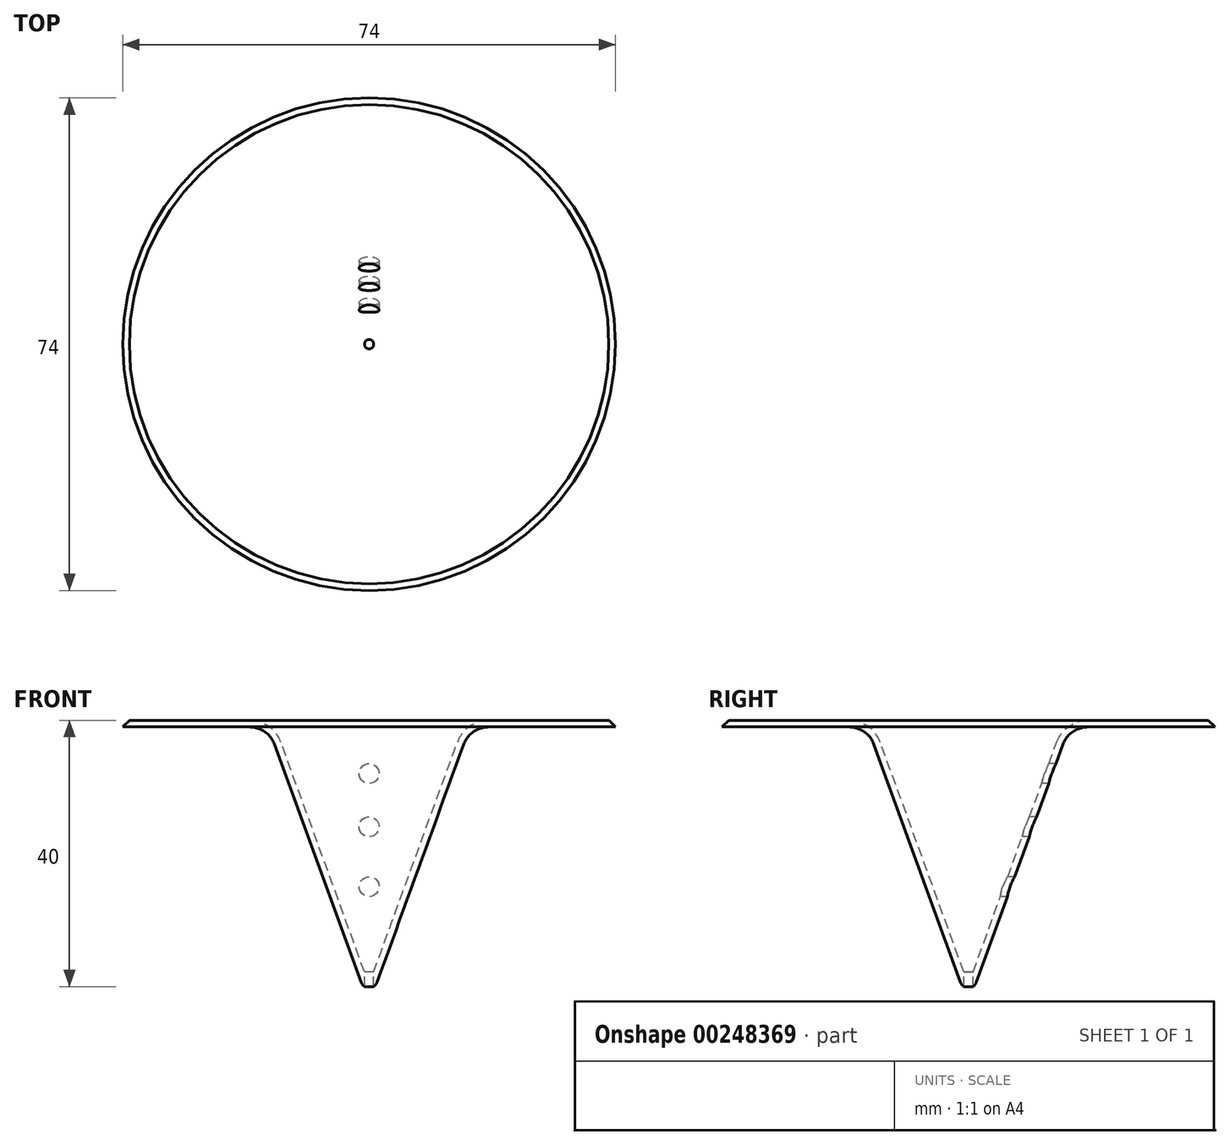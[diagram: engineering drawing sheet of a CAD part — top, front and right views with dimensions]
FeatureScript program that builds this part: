
annotation { "Feature Type Name" : "Feature", "Feature Type Description" : "" }
export const myFeature = defineFeature(function(context is Context, id is Id, definition is map)
    precondition{}
    {
        {
            var Q0;
            Q0=qCreatedBy(makeId("Front.planeOp"),FACE);
            var sketch = newSketch(context, id + "F0", { "sketchPlane" : qUnion([Q0])});
            skLineSegment(sketch, "E0", {"start": v(-36, 1) * mm, "end": v(-37, 0) * mm});
            skLineSegment(sketch, "E1", {"start": v(-37, 0) * mm, "end": v(-17.95, 0) * mm});
            skLineSegment(sketch, "E2", {"start": v(-36, 1) * mm, "end": v(-37, 1) * mm, "construction": true});
            skLineSegment(sketch, "E3", {"start": v(-37, 1) * mm, "end": v(-37, 0) * mm, "construction": true});
            skLineSegment(sketch, "E4.trimOffspring", {"start": v(-17.95, 1) * mm, "end": v(-36, 1) * mm});
            skArc(sketch, "E5", {"start": v(-1.17, -38.39) * mm, "mid": v(-0.98, -38.73) * mm, "end": v(-0.7, -39) * mm});
            skLineSegment(sketch, "E6", {"start": v(0, -34.13) * mm, "end": v(0, -39.21) * mm});
            skLineSegment(sketch, "E7", {"start": v(-0.7, -36.78) * mm, "end": v(-13.25, -2.29) * mm});
            skLineSegment(sketch, "E8", {"start": v(-1.17, -38.39) * mm, "end": v(-14.19, -2.63) * mm});
            skPoint(sketch, "E9.visualSharp", {"position": v(-15.15, 0) * mm});
            skArc(sketch, "E9.filletArc", {"start": v(-14.19, -2.63) * mm, "mid": v(-15.65, -0.72) * mm, "end": v(-17.95, 0) * mm});
            skPoint(sketch, "E10.visualSharp", {"position": v(-14.45, 1) * mm});
            skArc(sketch, "E10.filletArc", {"start": v(-13.25, -2.29) * mm, "mid": v(-15.08, 0.1) * mm, "end": v(-17.95, 1) * mm});
            skLineSegment(sketch, "E11", {"start": v(-0.7, -36.78) * mm, "end": v(-0.7, -39) * mm});
            skSolve(sketch);
        }
        {
            var Q0;
            Q0 = qSketchRegion(id + "F0", true);
            var Q1;
            Q1=sQuery(id+"F0.wireOp",EDGE,"E6");
            revolve(context, id + "F1", {"entities" : qUnion([Q0]), "axis" : qUnion([Q1]), "revolveType" : RevolveType.FULL});
        }
        {
            var Q0;
            Q0=qCreatedBy(makeId("Front.planeOp"),FACE);
            var sketch = newSketch(context, id + "F2", { "sketchPlane" : qUnion([Q0])});
            skPoint(sketch, "E12", {"position": v(0, -7) * mm});
            skPoint(sketch, "E13", {"position": v(0, -15) * mm});
            skPoint(sketch, "E14", {"position": v(0, -23) * mm});
            skSolve(sketch);
        }
        {
            var Q0;
            Q0=sQuery(id+"F2.wireOp",VERTEX,"E12");
            var Q1;
            Q1=makeQuery(id+"F1.opRevolve","SWEPT_BODY",BODY,{"disambiguationData":[OSD([sQuery(id+"F0.wireOp",EDGE,"E0"),sQuery(id+"F0.wireOp",EDGE,"E1"),sQuery(id+"F0.wireOp",EDGE,"yChOrPg3-cPpm-Jh2U-GKyL-P4V1HaA0gBOr"),sQuery(id+"F0.wireOp",EDGE,"y4288l65-jYWD-z8UQ-ppUS-tLJqPGtI5XHZ"),sQuery(id+"F0.wireOp",EDGE,"JWE7uGzO-epyR-hSJP-RyyS-bABGlfE59ylt"),sQuery(id+"F0.wireOp",EDGE,"iOWQaLnk-FQV4-ur3H-6gPm-ICKGlc5A2Xpd"),sQuery(id+"F0.wireOp",EDGE,"KzDe4Qk1-xao2-viCX-nbg6-8rSiEGRuAt0v"),sQuery(id+"F0.wireOp",EDGE,"b27d7dc2-f4b6-4ca7-adcb-c142e029c6df.trimOffspring"),sQuery(id+"F0.wireOp",EDGE,"ad9f041a-46d9-4f32-ac37-72ff34ba22ea.filletArc"),sQuery(id+"F0.wireOp",EDGE,"1201348b-4cfc-4bf2-a3ae-67f3a93fcbf4.filletArc"),sQuery(id+"F0.wireOp",EDGE,"f59c0a59-bad8-41fa-9d51-29288c238455.filletArc"),sQuery(id+"F0.wireOp",EDGE,"5a073df5-ce1a-4d9e-9ccd-e940f481835a.filletArc"),sQuery(id+"F0.wireOp",EDGE,"0fd173fc-3cb6-4043-b6d9-18548de36d7c.0"),sQuery(id+"F0.wireOp",EDGE,"0fd173fc-3cb6-4043-b6d9-18548de36d7c.1"),sQuery(id+"F0.wireOp",EDGE,"0fd173fc-3cb6-4043-b6d9-18548de36d7c.2"),sQuery(id+"F0.wireOp",EDGE,"0fd173fc-3cb6-4043-b6d9-18548de36d7c.3"),sQuery(id+"F0.wireOp",EDGE,"0fd173fc-3cb6-4043-b6d9-18548de36d7c.4"),sQuery(id+"F0.wireOp",EDGE,"E4.trimOffspring"),sQuery(id+"F0.wireOp",EDGE,"04d921bc-0581-4436-9bac-b51495f5e26a.filletArc"),sQuery(id+"F0.wireOp",EDGE,"f0a70462-13f2-40e4-b8fc-10729a1678a8.filletArc")])]});
            hole(context, id + "F3", {"style" : HoleStyle.SIMPLE, "endStyle" : HoleEndStyle.THROUGH, "holeDiameter" : 3 * mm, "tappedDepth" : 12 * mm, "tapClearance" : 3, "locations" : qUnion([Q0]), "scope" : qUnion([Q1])});
        }
        {
            var Q0;
            Q0=qCreatedBy(makeId("Front.planeOp"),FACE);
            var sketch = newSketch(context, id + "F4", { "sketchPlane" : qUnion([Q0])});
            skPoint(sketch, "E15", {"position": v(0, -24) * mm});
            skSolve(sketch);
        }
        {
            var Q0;
            Q0=sQuery(id+"F4.wireOp",VERTEX,"E15");
            var Q1;
            Q1=makeQuery(id+"F1.opRevolve","SWEPT_BODY",BODY,{"disambiguationData":[OSD([sQuery(id+"F0.wireOp",EDGE,"E0"),sQuery(id+"F0.wireOp",EDGE,"E1"),sQuery(id+"F0.wireOp",EDGE,"E4.trimOffspring"),sQuery(id+"F0.wireOp",EDGE,"E5"),sQuery(id+"F0.wireOp",EDGE,"E7"),sQuery(id+"F0.wireOp",EDGE,"E8"),sQuery(id+"F0.wireOp",EDGE,"E9.filletArc"),sQuery(id+"F0.wireOp",EDGE,"E10.filletArc"),sQuery(id+"F0.wireOp",EDGE,"E11")])]});
            hole(context, id + "F5", {"style" : HoleStyle.SIMPLE, "endStyle" : HoleEndStyle.THROUGH, "holeDiameter" : 3 * mm, "tappedDepth" : 12 * mm, "tapClearance" : 3, "locations" : qUnion([Q0]), "scope" : qUnion([Q1])});
        }
        {
            var Q0;
            Q0=qCreatedBy(makeId("Front.planeOp"),FACE);
            var sketch = newSketch(context, id + "F6", { "sketchPlane" : qUnion([Q0])});
            skPoint(sketch, "E16", {"position": v(0, -15) * mm});
            skSolve(sketch);
        }
        {
            var Q0;
            Q0=sQuery(id+"F6.wireOp",VERTEX,"E16");
            var Q1;
            Q1=makeQuery(id+"F1.opRevolve","SWEPT_BODY",BODY,{"disambiguationData":[OSD([sQuery(id+"F0.wireOp",EDGE,"E0"),sQuery(id+"F0.wireOp",EDGE,"E1"),sQuery(id+"F0.wireOp",EDGE,"E4.trimOffspring"),sQuery(id+"F0.wireOp",EDGE,"E5"),sQuery(id+"F0.wireOp",EDGE,"E7"),sQuery(id+"F0.wireOp",EDGE,"E8"),sQuery(id+"F0.wireOp",EDGE,"E9.filletArc"),sQuery(id+"F0.wireOp",EDGE,"E10.filletArc"),sQuery(id+"F0.wireOp",EDGE,"E11")])]});
            hole(context, id + "F7", {"style" : HoleStyle.SIMPLE, "endStyle" : HoleEndStyle.THROUGH, "holeDiameter" : 3 * mm, "tappedDepth" : 12 * mm, "tapClearance" : 3, "locations" : qUnion([Q0]), "scope" : qUnion([Q1])});
        }
    });
